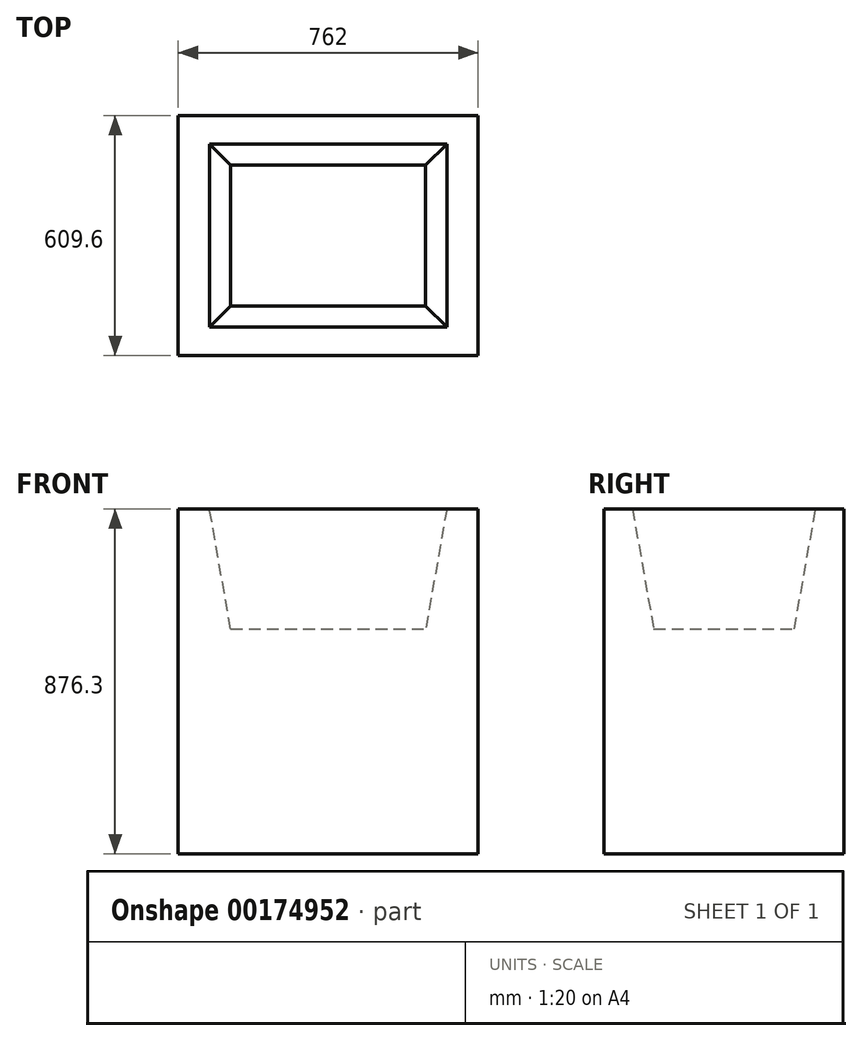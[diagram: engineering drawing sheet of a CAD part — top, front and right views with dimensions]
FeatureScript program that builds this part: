
annotation { "Feature Type Name" : "Feature", "Feature Type Description" : "" }
export const myFeature = defineFeature(function(context is Context, id is Id, definition is map)
    precondition{}
    {
        {
            var Q0;
            Q0=qCreatedBy(makeId("Top.planeOp"),FACE);
            var sketch = newSketch(context, id + "F0", { "sketchPlane" : qUnion([Q0])});
            skLineSegment(sketch, "E0.bottom", {"start": v(381, -304.8) * mm, "end": v(-381, -304.8) * mm});
            skLineSegment(sketch, "E0.top", {"start": v(381, 304.8) * mm, "end": v(-381, 304.8) * mm});
            skLineSegment(sketch, "E0.left", {"start": v(381, -304.8) * mm, "end": v(381, 304.8) * mm});
            skLineSegment(sketch, "E0.right", {"start": v(-381, -304.8) * mm, "end": v(-381, 304.8) * mm});
            skPoint(sketch, "E0.middle", {"position": v(0, 0) * mm});
            skSolve(sketch);
        }
        {
            var Q0;
            Q0=makeQuery(id+"F0.imprint","IMPRINT",FACE,{"disambiguationData":[TD([[makeQuery(id+"F0.imprint","IMPRINT",EDGE,{"derivedFrom":sQuery(id+"F0.wireOp",EDGE,"E0.bottom")}),-1.0]])]});
            extrude(context, id + "F1", {"entities" : qUnion([Q0]), "depth" : 876.3 * mm});
        }
        {
            var Q0;
            Q0=makeQuery(id+"F1.opExtrude","CAP_FACE",FACE,{"disambiguationData":[OSD([sQuery(id+"F0.wireOp",EDGE,"E0.bottom"),sQuery(id+"F0.wireOp",EDGE,"E0.top"),sQuery(id+"F0.wireOp",EDGE,"E0.left"),sQuery(id+"F0.wireOp",EDGE,"E0.right")])],"isStart":false});
            var sketch = newSketch(context, id + "F2", { "sketchPlane" : qUnion([Q0])});
            skLineSegment(sketch, "E1.bottom", {"start": v(301.3, -232.65) * mm, "end": v(-301.3, -232.65) * mm});
            skLineSegment(sketch, "E1.top", {"start": v(301.3, 232.65) * mm, "end": v(-301.3, 232.65) * mm});
            skLineSegment(sketch, "E1.left", {"start": v(301.3, -232.65) * mm, "end": v(301.3, 232.65) * mm});
            skLineSegment(sketch, "E1.right", {"start": v(-301.3, -232.65) * mm, "end": v(-301.3, 232.65) * mm});
            skPoint(sketch, "E1.middle", {"position": v(0, 0) * mm});
            skSolve(sketch);
        }
        {
            var Q0;
            Q0=makeQuery(id+"F2.imprint","IMPRINT",FACE,{"disambiguationData":[TD([[makeQuery(id+"F2.imprint","IMPRINT",EDGE,{"derivedFrom":sQuery(id+"F2.wireOp",EDGE,"E1.bottom")}),-1.0]])]});
            extrude(context, id + "F3", {"entities" : qUnion([Q0]), "operationType" : NewBodyOperationType.REMOVE, "oppositeDirection" : true, "depth" : 304.8 * mm, "hasDraft" : true, "draftAngle" : 10 * degree, "draftPullDirection" : true});
        }
    });
